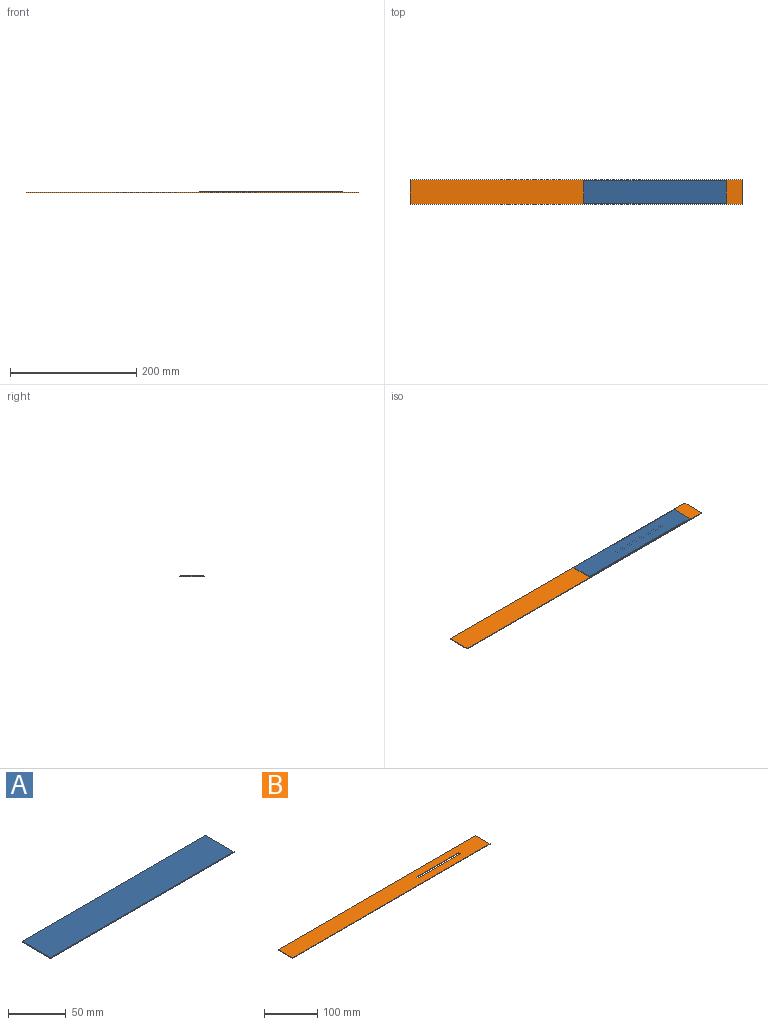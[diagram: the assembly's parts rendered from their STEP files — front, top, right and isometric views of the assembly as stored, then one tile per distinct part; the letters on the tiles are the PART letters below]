
ASSEMBLY  parts=2 mates=1
PART A: 6 faces, bbox 225x35x1 mm
  f0: plane 225x1mm, normal (0,1,0), area 225mm2, adj f1,f3,f4,f5
  f1: plane 35x1mm, normal (-1,0,0), area 35mm2, adj f0,f2,f4,f5
  f2: plane 225x1mm, normal (0,-1,0), area 225mm2, adj f1,f3,f4,f5
  f3: plane 35x1mm, normal (1,0,0), area 35mm2, adj f0,f2,f4,f5
  f4: plane 225x35mm, normal (0,0,1), area 7875mm2, adj f0,f1,f2,f3
  f5: plane 225x35mm, normal (0,0,-1), area 7875mm2, adj f0,f1,f2,f3
PART B: 10 faces, bbox 525x38x1 mm
  f0: plane 525x1mm, normal (0,1,0), area 525mm2, adj f1,f3,f4,f5
  f1: plane 38x1mm, normal (-1,0,0), area 38mm2, adj f0,f2,f4,f5
  f2: plane 525x1mm, normal (0,-1,0), area 525mm2, adj f1,f3,f4,f5
  f3: plane 38x1mm, normal (1,0,0), area 38mm2, adj f0,f2,f4,f5
  f4: plane 525x38mm, normal (0,0,1), area 19502mm2, adj f0,f1,f2,f3,f6,f7,f8,f9
  f5: plane 525x38mm, normal (0,0,-1), area 19502mm2, adj f0,f1,f2,f3,f6,f7,f8,f9
  f6: plane 4x1mm, normal (1,0,0), area 4mm2, adj f4,f5,f7,f9
  f7: plane 112x1mm, normal (0,1,0), area 112mm2, adj f4,f5,f6,f8
  f8: plane 4x1mm, normal (-1,0,0), area 4mm2, adj f4,f5,f7,f9
  f9: plane 112x1mm, normal (0,-1,0), area 112mm2, adj f4,f5,f6,f8
PLACE A at identity
PLACE B t=(-125,0,-1)mm
MATE fastened B.f4 <-> A.f5  axis (0,0,1) through (137,0,0)mm
